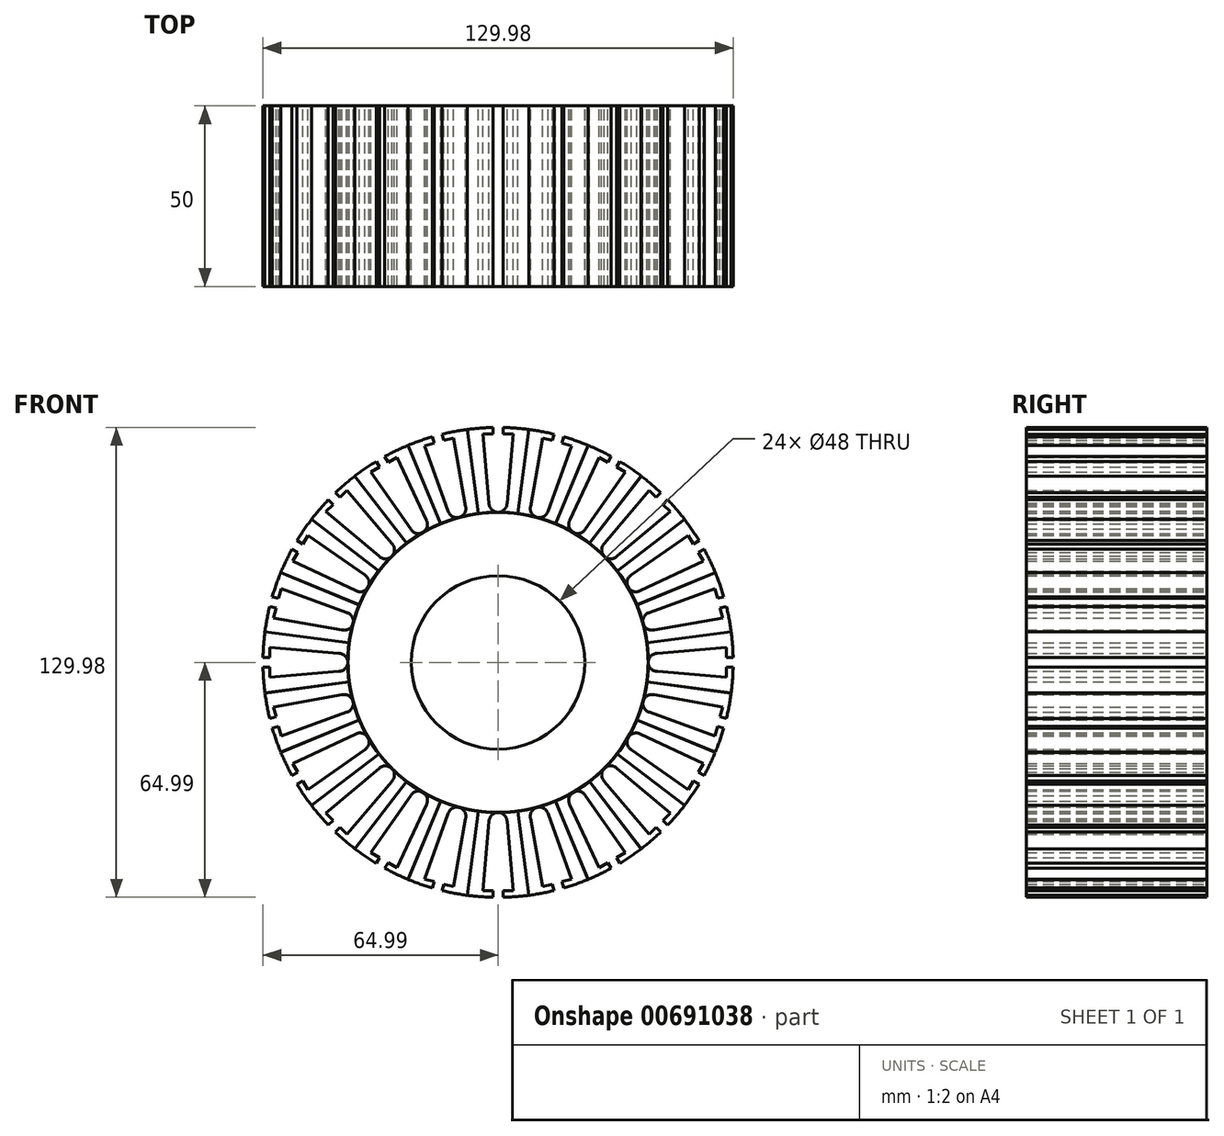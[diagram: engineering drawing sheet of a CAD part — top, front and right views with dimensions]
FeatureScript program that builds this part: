
annotation { "Feature Type Name" : "Feature", "Feature Type Description" : "" }
export const myFeature = defineFeature(function(context is Context, id is Id, definition is map)
    precondition{}
    {
        {
            var Q0;
            Q0=qCreatedBy(makeId("Front.planeOp"),FACE);
            var sketch = newSketch(context, id + "F0", { "sketchPlane" : qUnion([Q0])});
            skArc(sketch, "E0", {"start": v(-5.42, 41.18) * mm, "mid": v(0, -41.53) * mm, "end": v(5.42, 41.18) * mm});
            skArc(sketch, "E1", {"start": v(-2.49, 44.02) * mm, "mid": v(0, 41.53) * mm, "end": v(2.49, 44.02) * mm});
            skLineSegment(sketch, "E2", {"start": v(1.37, 63.16) * mm, "end": v(4.15, 63.16) * mm});
            skLineSegment(sketch, "E3", {"start": v(-1.37, 63.16) * mm, "end": v(-1.37, 64.99) * mm});
            skLineSegment(sketch, "E4.MirrorCS", {"start": v(1.37, 63.16) * mm, "end": v(1.37, 64.99) * mm});
            skLineSegment(sketch, "E5.MirrorCS", {"start": v(-1.37, 63.16) * mm, "end": v(-4.15, 63.16) * mm});
            skLineSegment(sketch, "E6", {"start": v(4.15, 63.16) * mm, "end": v(2.49, 44.02) * mm});
            skLineSegment(sketch, "E7", {"start": v(-2.49, 44.02) * mm, "end": v(-4.15, 63.16) * mm});
            skLineSegment(sketch, "E8", {"start": v(5.42, 41.18) * mm, "end": v(8.48, 64.44) * mm});
            skLineSegment(sketch, "E9", {"start": v(-5.42, 41.18) * mm, "end": v(-8.48, 64.44) * mm});
            skCircle(sketch, "E10", {"center": v(0, 0) * mm, "radius": 24 * mm});
            skArc(sketch, "E11", {"start": v(-1.38, 64.99) * mm, "mid": v(-4.93, 64.81) * mm, "end": v(-8.48, 64.44) * mm});
            skArc(sketch, "E12.trimOffspring", {"start": v(8.48, 64.44) * mm, "mid": v(4.93, 64.81) * mm, "end": v(1.37, 64.99) * mm});
            skSolve(sketch);
        }
        {
            var Q0;
            Q0 = qSketchRegion(id + "F0", true);
            extrude(context, id + "F1", {"entities" : qUnion([Q0]), "depth" : 50 * mm, "offsetDistance" : 25 * mm});
        }
        {
            var Q0;
            Q0=makeQuery(id+"F1.opExtrude","SWEPT_BODY",BODY,{"disambiguationData":[OSD([sQuery(id+"F0.wireOp",EDGE,"E0"),sQuery(id+"F0.wireOp",EDGE,"E1"),sQuery(id+"F0.wireOp",EDGE,"E2"),sQuery(id+"F0.wireOp",EDGE,"E3"),sQuery(id+"F0.wireOp",EDGE,"E4.MirrorCS"),sQuery(id+"F0.wireOp",EDGE,"E5.MirrorCS"),sQuery(id+"F0.wireOp",EDGE,"E6"),sQuery(id+"F0.wireOp",EDGE,"E7"),sQuery(id+"F0.wireOp",EDGE,"E8"),sQuery(id+"F0.wireOp",EDGE,"E9"),sQuery(id+"F0.wireOp",EDGE,"E10"),sQuery(id+"F0.wireOp",EDGE,"E11"),sQuery(id+"F0.wireOp",EDGE,"E12.trimOffspring")])]});
            var Q1;
            Q1=makeQuery(id+"F1.opExtrude","SWEPT_FACE",FACE,{"disambiguationData":[OSD([sQuery(id+"F0.wireOp",EDGE,"E0")])]});
            circularPattern(context, id + "F2", {"entities" : qUnion([Q0]), "axis" : qUnion([Q1]), "angle" : 360 * degree, "instanceCount" : 24, "equalSpace" : true});
        }
    });
